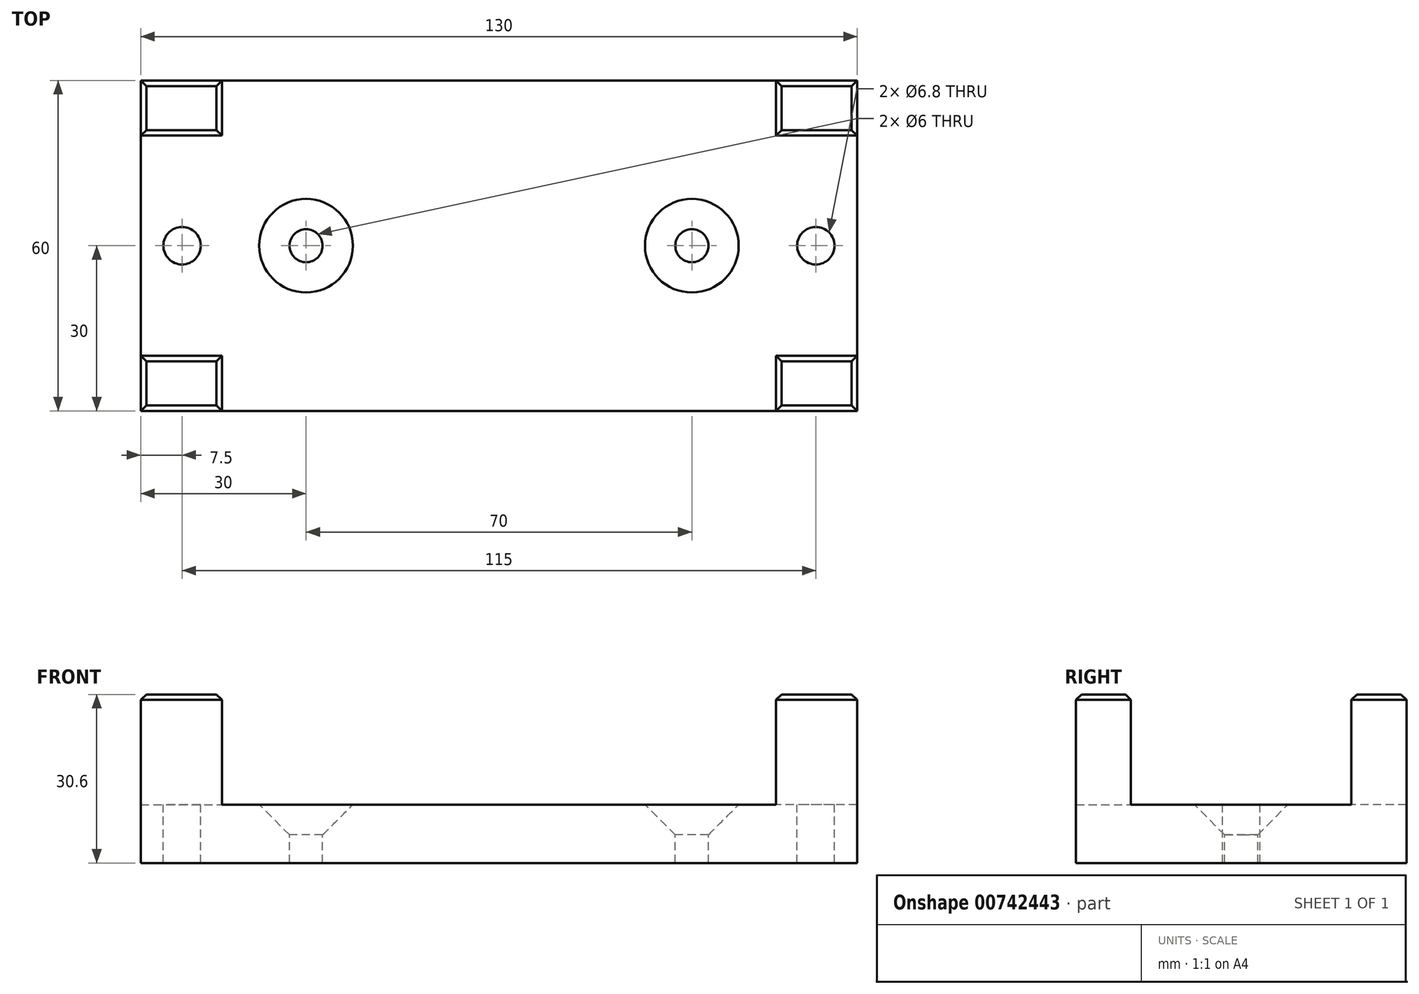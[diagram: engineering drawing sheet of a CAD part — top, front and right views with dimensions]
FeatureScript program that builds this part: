
annotation { "Feature Type Name" : "Feature", "Feature Type Description" : "" }
export const myFeature = defineFeature(function(context is Context, id is Id, definition is map)
    precondition{}
    {
        {
            var Q0;
            Q0=qCreatedBy(makeId("Top.planeOp"),FACE);
            var sketch = newSketch(context, id + "F0", { "sketchPlane" : qUnion([Q0])});
            skLineSegment(sketch, "E0.bottom", {"start": v(65, -30) * mm, "end": v(-65, -30) * mm});
            skLineSegment(sketch, "E0.top", {"start": v(65, 30) * mm, "end": v(-65, 30) * mm});
            skLineSegment(sketch, "E0.left", {"start": v(65, -30) * mm, "end": v(65, 30) * mm});
            skLineSegment(sketch, "E0.right", {"start": v(-65, -30) * mm, "end": v(-65, 30) * mm});
            skPoint(sketch, "E0.middle", {"position": v(0, 0) * mm});
            skSolve(sketch);
        }
        {
            var Q0;
            Q0=makeQuery(id+"F0.imprint","IMPRINT",FACE,{"disambiguationData":[TD([[makeQuery(id+"F0.imprint","IMPRINT",EDGE,{"derivedFrom":sQuery(id+"F0.wireOp",EDGE,"E0.bottom")}),-1.0]])]});
            extrude(context, id + "F1", {"entities" : qUnion([Q0]), "depth" : 10.6 * mm, "offsetDistance" : 25 * mm});
        }
        {
            var Q0;
            Q0=makeQuery(id+"F1.opExtrude","CAP_FACE",FACE,{"disambiguationData":[OSD([sQuery(id+"F0.wireOp",EDGE,"E0.bottom"),sQuery(id+"F0.wireOp",EDGE,"E0.top"),sQuery(id+"F0.wireOp",EDGE,"E0.left"),sQuery(id+"F0.wireOp",EDGE,"E0.right")])],"isStart":false});
            var sketch = newSketch(context, id + "F2", { "sketchPlane" : qUnion([Q0])});
            skLineSegment(sketch, "E1.bottom", {"start": v(-65, 30) * mm, "end": v(-50.25, 30) * mm});
            skLineSegment(sketch, "E1.top", {"start": v(-65, 20) * mm, "end": v(-50.25, 20) * mm});
            skLineSegment(sketch, "E1.left", {"start": v(-65, 30) * mm, "end": v(-65, 20) * mm});
            skLineSegment(sketch, "E1.right", {"start": v(-50.25, 30) * mm, "end": v(-50.25, 20) * mm});
            skLineSegment(sketch, "E2.bottom", {"start": v(65, 30) * mm, "end": v(50.25, 30) * mm});
            skLineSegment(sketch, "E2.top", {"start": v(65, 20) * mm, "end": v(50.25, 20) * mm});
            skLineSegment(sketch, "E2.left", {"start": v(65, 30) * mm, "end": v(65, 20) * mm});
            skLineSegment(sketch, "E2.right", {"start": v(50.25, 30) * mm, "end": v(50.25, 20) * mm});
            skLineSegment(sketch, "E3.bottom", {"start": v(65, -30) * mm, "end": v(50.25, -30) * mm});
            skLineSegment(sketch, "E3.top", {"start": v(65, -20) * mm, "end": v(50.25, -20) * mm});
            skLineSegment(sketch, "E3.left", {"start": v(65, -30) * mm, "end": v(65, -20) * mm});
            skLineSegment(sketch, "E3.right", {"start": v(50.25, -30) * mm, "end": v(50.25, -20) * mm});
            skLineSegment(sketch, "E4.bottom", {"start": v(-65, -30) * mm, "end": v(-50.25, -30) * mm});
            skLineSegment(sketch, "E4.top", {"start": v(-65, -20) * mm, "end": v(-50.25, -20) * mm});
            skLineSegment(sketch, "E4.left", {"start": v(-65, -30) * mm, "end": v(-65, -20) * mm});
            skLineSegment(sketch, "E4.right", {"start": v(-50.25, -30) * mm, "end": v(-50.25, -20) * mm});
            skSolve(sketch);
        }
        {
            var Q0;
            Q0=makeQuery(id+"F2.imprint","IMPRINT",FACE,{"disambiguationData":[TD([[makeQuery(id+"F2.imprint","IMPRINT",EDGE,{"derivedFrom":sQuery(id+"F2.wireOp",EDGE,"E1.bottom")}),1.0]])]});
            var Q1;
            Q1=makeQuery(id+"F2.imprint","IMPRINT",FACE,{"disambiguationData":[TD([[makeQuery(id+"F2.imprint","IMPRINT",EDGE,{"derivedFrom":sQuery(id+"F2.wireOp",EDGE,"E4.bottom")}),-1.0]])]});
            var Q2;
            Q2=makeQuery(id+"F2.imprint","IMPRINT",FACE,{"disambiguationData":[TD([[makeQuery(id+"F2.imprint","IMPRINT",EDGE,{"derivedFrom":sQuery(id+"F2.wireOp",EDGE,"E3.bottom")}),-1.0]])]});
            var Q3;
            Q3=makeQuery(id+"F2.imprint","IMPRINT",FACE,{"disambiguationData":[TD([[makeQuery(id+"F2.imprint","IMPRINT",EDGE,{"derivedFrom":sQuery(id+"F2.wireOp",EDGE,"E2.bottom")}),1.0]])]});
            extrude(context, id + "F3", {"entities" : qUnion([Q0, Q1, Q2, Q3]), "operationType" : NewBodyOperationType.ADD, "depth" : 20 * mm, "offsetDistance" : 25 * mm});
        }
        {
            var Q0;
            Q0=makeQuery(id+"F1.opExtrude","CAP_FACE",FACE,{"disambiguationData":[OSD([sQuery(id+"F0.wireOp",EDGE,"E0.bottom"),sQuery(id+"F0.wireOp",EDGE,"E0.top"),sQuery(id+"F0.wireOp",EDGE,"E0.left"),sQuery(id+"F0.wireOp",EDGE,"E0.right")])],"isStart":false});
            var sketch = newSketch(context, id + "F4", { "sketchPlane" : qUnion([Q0])});
            skPoint(sketch, "E5", {"position": v(57.5, 0) * mm});
            skPoint(sketch, "E5.positionSnap0", {"position": v(65, 0) * mm});
            skPoint(sketch, "E6", {"position": v(-57.5, 0) * mm});
            skSolve(sketch);
        }
        {
            var Q0;
            Q0=sQuery(id+"F4.wireOp",VERTEX,"E5");
            var Q1;
            Q1=sQuery(id+"F4.wireOp",VERTEX,"E6");
            var Q2;
            Q2=makeQuery(id+"F1.opExtrude","SWEPT_BODY",BODY,{"disambiguationData":[OSD([sQuery(id+"F0.wireOp",EDGE,"E0.bottom"),sQuery(id+"F0.wireOp",EDGE,"E0.top"),sQuery(id+"F0.wireOp",EDGE,"E0.left"),sQuery(id+"F0.wireOp",EDGE,"E0.right")])]});
            hole(context, id + "F5", {"style" : HoleStyle.SIMPLE, "endStyle" : HoleEndStyle.THROUGH, "standardTappedOrClearance" : lookupTablePath({ "standard" : "ISO", "engagement" : "75%", "pitch" : "1.25 mm", "size" : "M8", "type" : "Tapped" }), "standardBlindInLast" : lookupTablePath({ "standard" : "ISO", "engagement" : "75%", "pitch" : "1.25 mm", "size" : "M8", "type" : "Tapped" }), "holeDiameter" : 6.8 * mm, "majorDiameter" : 8 * mm, "showTappedDepth" : true, "isTappedThrough" : true, "tappedDepth" : 30 * mm, "tapClearance" : 0, "startFromSketch" : true, "locations" : qUnion([Q0, Q1]), "scope" : qUnion([Q2])});
        }
        {
            var Q0;
            Q0=makeQuery(id+"F1.opExtrude","CAP_FACE",FACE,{"disambiguationData":[OSD([sQuery(id+"F0.wireOp",EDGE,"E0.bottom"),sQuery(id+"F0.wireOp",EDGE,"E0.top"),sQuery(id+"F0.wireOp",EDGE,"E0.left"),sQuery(id+"F0.wireOp",EDGE,"E0.right")])],"isStart":false});
            var sketch = newSketch(context, id + "F6", { "sketchPlane" : qUnion([Q0])});
            skPoint(sketch, "E7", {"position": v(35, 0) * mm});
            skPoint(sketch, "E7.positionSnap0", {"position": v(65, 0) * mm});
            skPoint(sketch, "E8", {"position": v(-35, 0) * mm});
            skSolve(sketch);
        }
        {
            var Q0;
            Q0=sQuery(id+"F6.wireOp",VERTEX,"E7");
            var Q1;
            Q1=sQuery(id+"F6.wireOp",VERTEX,"E8");
            var Q2;
            Q2=makeQuery(id+"F1.opExtrude","SWEPT_BODY",BODY,{"disambiguationData":[OSD([sQuery(id+"F0.wireOp",EDGE,"E0.bottom"),sQuery(id+"F0.wireOp",EDGE,"E0.top"),sQuery(id+"F0.wireOp",EDGE,"E0.left"),sQuery(id+"F0.wireOp",EDGE,"E0.right")])]});
            hole(context, id + "F7", {"style" : HoleStyle.C_SINK, "endStyle" : HoleEndStyle.THROUGH, "standardTappedOrClearance" : lookupTablePath({ "standard" : "ISO", "size" : "6", "type" : "Drilled" }), "standardBlindInLast" : lookupTablePath({ "standard" : "ISO", "size" : "6", "type" : "Drilled" }), "holeDiameter" : 6 * mm, "cSinkDiameter" : 17 * mm, "cSinkAngle" : 90 * degree, "majorDiameter" : 8 * mm, "isTappedThrough" : true, "tappedDepth" : 30 * mm, "tapClearance" : 0, "startFromSketch" : true, "locations" : qUnion([Q0, Q1]), "scope" : qUnion([Q2])});
        }
        {
            var Q0;
            Q0=makeQuery(id+"F3.opExtrude","CAP_EDGE",EDGE,{"disambiguationData":[OSD([sQuery(id+"F2.wireOp",EDGE,"E4.bottom")])],"isStart":false});
            var Q1;
            Q1=makeQuery(id+"F3.opExtrude","CAP_EDGE",EDGE,{"disambiguationData":[OSD([sQuery(id+"F2.wireOp",EDGE,"E4.right")])],"isStart":false});
            var Q2;
            Q2=makeQuery(id+"F3.opExtrude","CAP_EDGE",EDGE,{"disambiguationData":[OSD([sQuery(id+"F2.wireOp",EDGE,"E4.top")])],"isStart":false});
            var Q3;
            Q3=makeQuery(id+"F3.opExtrude","CAP_EDGE",EDGE,{"disambiguationData":[OSD([sQuery(id+"F2.wireOp",EDGE,"E4.left")])],"isStart":false});
            var Q4;
            Q4=makeQuery(id+"F3.opExtrude","CAP_EDGE",EDGE,{"disambiguationData":[OSD([sQuery(id+"F2.wireOp",EDGE,"E1.top")])],"isStart":false});
            var Q5;
            Q5=makeQuery(id+"F3.opExtrude","CAP_EDGE",EDGE,{"disambiguationData":[OSD([sQuery(id+"F2.wireOp",EDGE,"E1.bottom")])],"isStart":false});
            var Q6;
            Q6=makeQuery(id+"F3.opExtrude","CAP_EDGE",EDGE,{"disambiguationData":[OSD([sQuery(id+"F2.wireOp",EDGE,"E1.right")])],"isStart":false});
            var Q7;
            Q7=makeQuery(id+"F3.opExtrude","CAP_EDGE",EDGE,{"disambiguationData":[OSD([sQuery(id+"F2.wireOp",EDGE,"E1.left")])],"isStart":false});
            var Q8;
            Q8=makeQuery(id+"F3.opExtrude","CAP_EDGE",EDGE,{"disambiguationData":[OSD([sQuery(id+"F2.wireOp",EDGE,"E3.right")])],"isStart":false});
            var Q9;
            Q9=makeQuery(id+"F3.opExtrude","CAP_EDGE",EDGE,{"disambiguationData":[OSD([sQuery(id+"F2.wireOp",EDGE,"E3.top")])],"isStart":false});
            var Q10;
            Q10=makeQuery(id+"F3.opExtrude","CAP_EDGE",EDGE,{"disambiguationData":[OSD([sQuery(id+"F2.wireOp",EDGE,"E3.left")])],"isStart":false});
            var Q11;
            Q11=makeQuery(id+"F3.opExtrude","CAP_EDGE",EDGE,{"disambiguationData":[OSD([sQuery(id+"F2.wireOp",EDGE,"E3.bottom")])],"isStart":false});
            var Q12;
            Q12=makeQuery(id+"F3.opExtrude","CAP_EDGE",EDGE,{"disambiguationData":[OSD([sQuery(id+"F2.wireOp",EDGE,"E2.left")])],"isStart":false});
            var Q13;
            Q13=makeQuery(id+"F3.opExtrude","CAP_EDGE",EDGE,{"disambiguationData":[OSD([sQuery(id+"F2.wireOp",EDGE,"E2.top")])],"isStart":false});
            var Q14;
            Q14=makeQuery(id+"F3.opExtrude","CAP_EDGE",EDGE,{"disambiguationData":[OSD([sQuery(id+"F2.wireOp",EDGE,"E2.right")])],"isStart":false});
            var Q15;
            Q15=makeQuery(id+"F3.opExtrude","CAP_EDGE",EDGE,{"disambiguationData":[OSD([sQuery(id+"F2.wireOp",EDGE,"E2.bottom")])],"isStart":false});
            chamfer(context, id + "F8", {"entities" : qUnion([Q0, Q1, Q2, Q3, Q4, Q5, Q6, Q7, Q8, Q9, Q10, Q11, Q12, Q13, Q14, Q15]), "width" : 1 * mm, "tangentPropagation" : true});
        }
    });
